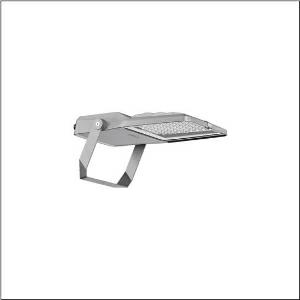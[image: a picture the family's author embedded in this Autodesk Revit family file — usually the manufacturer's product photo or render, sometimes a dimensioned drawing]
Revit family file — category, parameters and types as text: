
# Revit family: floodlight_fl_21_mini___pl64_5xa7771b2e1a_5ce5
name_source: partatom
category: Lighting Fixtures
units: mm (PartAtom-declared; Revit-internal decimal feet)

## family parameters
Cut with Voids When Loaded = No
Host = Face
Light Source = No
Part Type = Normal
Room Calculation Point = No
Round Connector Dimension = Use Diameter
Shared = No

## types (1)
- --- (1 x LED, 6020 lm, 45.5 W, 3000K)
    Apparent Load = 46 VA
    CIE Flux Codes = 28 80 98 100 100
    Color Rendering = 70
    Color Temperature = 3000K
    Default Elevation = 1800 mm
    Description = Floodlight FL 21 mini, floodlight, primary light control with lens, of PMMA, primary optical cover: protective disc, of toughened safety glass, transparent, light distribution: PL64, light emission: direct distribution, installation type: surface-mounted, LED, High Power LED, rated luminous flux: 6.020lm, luminous efficacy: 132lm/W, light colour: 730, colour temperature: 3000K, control gear: ECG iQ, control: Auto-Match, Temp-Guard, Lumen-Switch, Night-Set, Smart-Wire, Light-Fading, Desk-Remote (wireless, voltage-free reading and setting of iQ features in the workshop via application-optimized NFC function/RFID function), optimised constant luminous flux control (CLO 2.0), with terminal, 6-pole, mains connection: 220..240V, AC, 50/60Hz, start of lifetime: 46W, end of lifetime: 48W, reduction: 22W, luminaire housing, of diecast aluminium, powder-coated, Siteco® metallic grey (DB 702S), corrosivity category C5 according to DIN EN ISO 12944, mounting bracket, of steel, galvanised, powder-coated, Siteco® metallic grey (DB 702S), protection rating (complete): IP66, insulation class (complete): insulation class II (safety insulation), certification: CE, ENEC, VDE, protection symbol: D, impact resistance: IK08, permissible operating ambient temperature: -40..+40°C, permissible operating ambient temperature for outdoor applications: -40..+50°C, standard: DIN EN 12944, packaging unit: 1 piece

Light Distribution: PL64
    Height = 70 mm
    Lamp = 1 x LED
    Lamp Light Flux = 6020 lm
    Lamp Power = 45.5 W
    Lamp count = 1
    Length = 485 mm
    Luminous efficacy = 132 lm/W
    Manufacturer = Siteco
    ModVariant = No
    Model = 5XA7771B2E1A
    Number of Poles = 1
    OnlyDefault = Yes
    Power Factor = 1
    Product Name = Floodlight FL 21 mini | PL64
    Product group = floodlight | pylon top
    ProductGroupID = 6101
    Protection Class = Protection class II
    Protection Degree = IP 66
    RLX_Detail_Level = 1
    RlxData = <blob elided: 96009 chars, md5=a81954c9>
    Socket = socket
    Standby Power = 0 W
    System Light Flux = 6020 lm
    System Power = 46 W
    Type Comments = factory setting: luminous flux: 100 % | dim-lin: 254 | 463 mA
    Type Image = l_1006845.jpg
    URL = http://relux.com
    VarID = @adj_078277
    Voltage = 0 V
    Weight = 0.00 kg
    Width = 337 mm

## geometry (parser evidence)
native form markers: Blend x4, Sweep x12
no freeform markers — native parametric forms only
